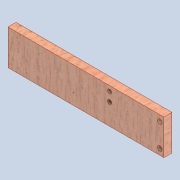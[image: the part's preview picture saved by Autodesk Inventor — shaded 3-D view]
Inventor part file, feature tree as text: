
AUTODESK INVENTOR PART (.ipt)
format: ipt  version: 2020 (Build 240168000, 168)  size: 173,056 bytes
history: native  units: mm
features: hole x2, sketch x2, extrude x1
ambient origin geometry x8: Origin, YZ Plane, XZ Plane, XY Plane, X Axis, Y Axis, Z Axis, Center Point
bodies: Solid1 (feature_tree)
feature tree (5):
  extrude  "Extrusion1"  Depth=35.0mm
  hole  "Hole1"  [1 undecoded]
  hole  "Hole2"  [1 undecoded]
  sketch  "Sketch1"  dims[d0=155.0mm d1=35.0mm]
  sketch  "Sketch4"  dims[d2=8.0mm d3=0.0mm d19=4.0mm d20=6.0mm d21=4.5mm d22=6.0mm d23=4.0mm d24=2.0mm d25=90.0deg d26=8.0mm d27=20.594885mm d28=4.0mm d29=6.0mm d30=4.0mm d31=2.0mm d32=90.0deg d33=8.0mm d34=20.594885mm]
note: 2 required parameter values undecoded (feature->parameter linkage not recoverable at this tier; creation-order binding heuristic only, values carry confidence <= 0.55)
